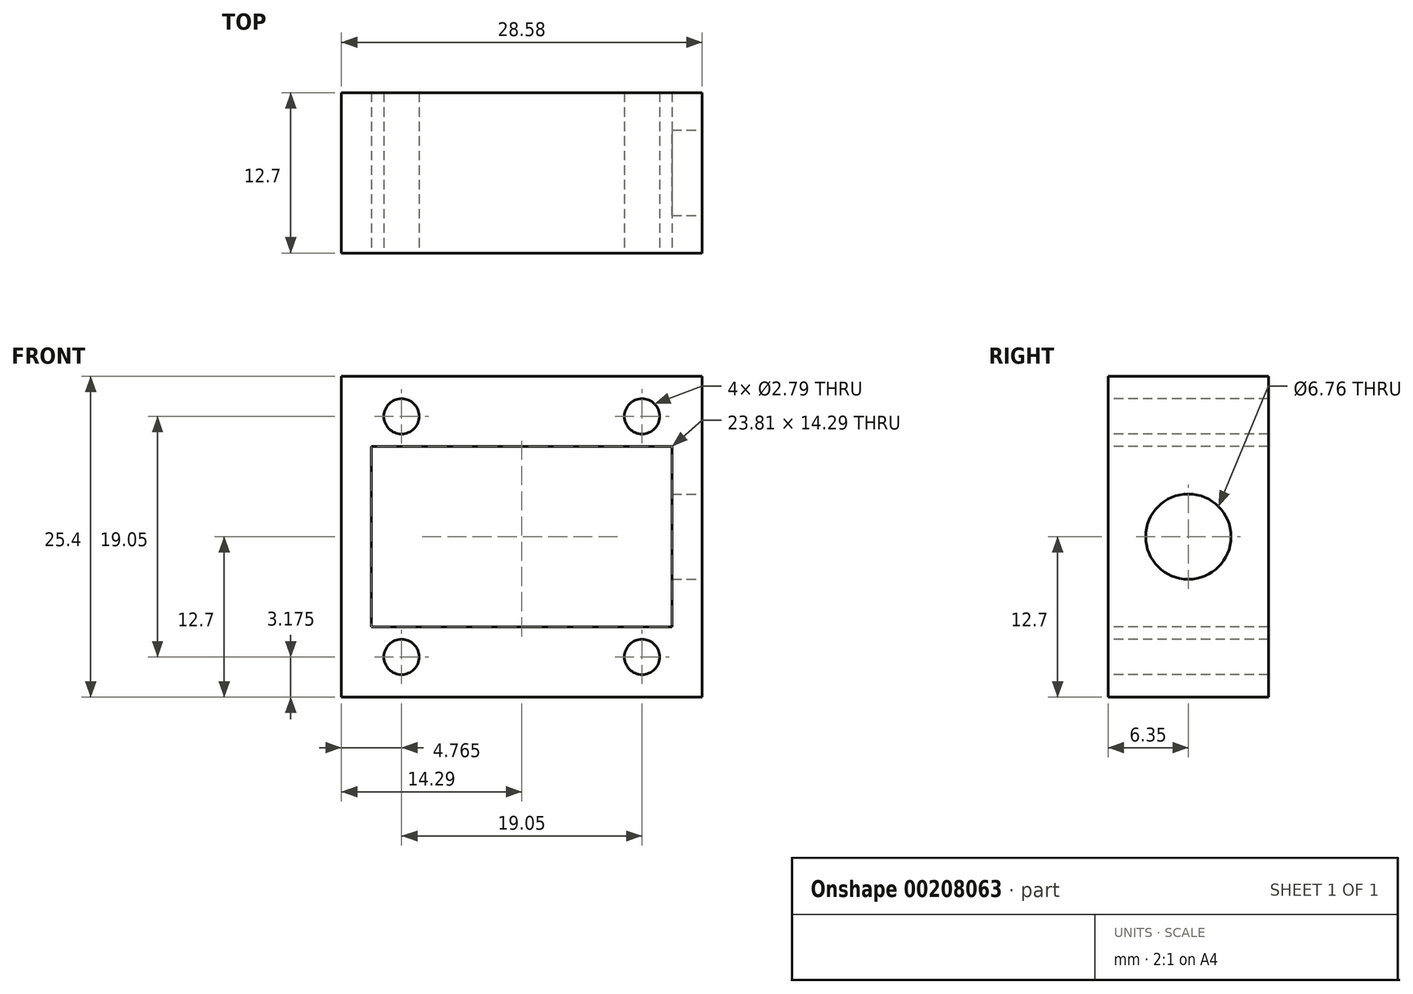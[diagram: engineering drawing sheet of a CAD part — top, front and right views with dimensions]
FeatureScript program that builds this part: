
annotation { "Feature Type Name" : "Feature", "Feature Type Description" : "" }
export const myFeature = defineFeature(function(context is Context, id is Id, definition is map)
    precondition{}
    {
        {
            var Q0;
            Q0=qCreatedBy(makeId("Front.planeOp"),FACE);
            var sketch = newSketch(context, id + "F0", { "sketchPlane" : qUnion([Q0])});
            skLineSegment(sketch, "E0.bottom", {"start": v(14.29, -12.7) * mm, "end": v(-14.29, -12.7) * mm});
            skLineSegment(sketch, "E0.top", {"start": v(14.29, 12.7) * mm, "end": v(-14.29, 12.7) * mm});
            skLineSegment(sketch, "E0.left", {"start": v(14.29, -12.7) * mm, "end": v(14.29, 12.7) * mm});
            skLineSegment(sketch, "E0.right", {"start": v(-14.29, -12.7) * mm, "end": v(-14.29, 12.7) * mm});
            skPoint(sketch, "E0.middle", {"position": v(0, 0) * mm});
            skSolve(sketch);
        }
        {
            var Q0;
            Q0 = qSketchRegion(id + "F0", true);
            extrude(context, id + "F1", {"entities" : qUnion([Q0]), "depth" : 12.7 * mm});
        }
        {
            var Q0;
            Q0=makeQuery(id+"F1.opExtrude","CAP_FACE",FACE,{"disambiguationData":[OSD([sQuery(id+"F0.wireOp",EDGE,"E0.bottom"),sQuery(id+"F0.wireOp",EDGE,"E0.top"),sQuery(id+"F0.wireOp",EDGE,"E0.left"),sQuery(id+"F0.wireOp",EDGE,"E0.right")])],"isStart":false});
            var sketch = newSketch(context, id + "F2", { "sketchPlane" : qUnion([Q0])});
            skLineSegment(sketch, "E1.bottom", {"start": v(11.9, -7.14) * mm, "end": v(-11.9, -7.14) * mm});
            skLineSegment(sketch, "E1.top", {"start": v(11.9, 7.14) * mm, "end": v(-11.9, 7.14) * mm});
            skLineSegment(sketch, "E1.left", {"start": v(11.9, -7.14) * mm, "end": v(11.9, 7.14) * mm});
            skLineSegment(sketch, "E1.right", {"start": v(-11.9, -7.14) * mm, "end": v(-11.9, 7.14) * mm});
            skPoint(sketch, "E1.middle", {"position": v(0, 0) * mm});
            skSolve(sketch);
        }
        {
            var Q0;
            Q0 = qSketchRegion(id + "F2", true);
            extrude(context, id + "F3", {"entities" : qUnion([Q0]), "operationType" : NewBodyOperationType.REMOVE, "endBound" : BoundingType.THROUGH_ALL, "oppositeDirection" : true, "depth" : 25.4 * mm});
        }
        {
            var Q0;
            Q0=makeQuery(id+"F1.opExtrude","SWEPT_FACE",FACE,{"disambiguationData":[OSD([sQuery(id+"F0.wireOp",EDGE,"E0.left")])]});
            var sketch = newSketch(context, id + "F4", { "sketchPlane" : qUnion([Q0])});
            skPoint(sketch, "E2", {"position": v(-6.35, 0) * mm});
            skLineSegment(sketch, "E3", {"start": v(-6.35, 0) * mm, "end": v(0, 0) * mm});
            skLineSegment(sketch, "E4", {"start": v(-6.35, 0) * mm, "end": v(-12.7, 0) * mm});
            skSolve(sketch);
        }
        {
            var Q0;
            Q0=sQuery(id+"F4.wireOp",VERTEX,"E2");
            var Q1;
            Q1=makeQuery(id+"F1.opExtrude","SWEPT_BODY",BODY,{"disambiguationData":[OSD([sQuery(id+"F0.wireOp",EDGE,"E0.bottom"),sQuery(id+"F0.wireOp",EDGE,"E0.top"),sQuery(id+"F0.wireOp",EDGE,"E0.left"),sQuery(id+"F0.wireOp",EDGE,"E0.right")])]});
            hole(context, id + "F5", {"style" : HoleStyle.SIMPLE, "endStyle" : HoleEndStyle.BLIND, "standardTappedOrClearance" : lookupTablePath({ "standard" : "ANSI", "fit" : "Normal (ASME)", "size" : "1/4", "type" : "Clearance" }), "standardBlindInLast" : lookupTablePath({ "fit" : "Free", "standard" : "ANSI", "size" : "1/4", "type" : "Clearance" }), "holeDiameter" : 6.76 * mm, "holeDepth" : 3.97 * mm, "tappedDepth" : 1.59 * mm, "tapClearance" : 3, "locations" : qUnion([Q0]), "scope" : qUnion([Q1])});
        }
        {
            var Q0;
            Q0=makeQuery(id+"F1.opExtrude","CAP_FACE",FACE,{"disambiguationData":[OSD([sQuery(id+"F0.wireOp",EDGE,"E0.bottom"),sQuery(id+"F0.wireOp",EDGE,"E0.top"),sQuery(id+"F0.wireOp",EDGE,"E0.left"),sQuery(id+"F0.wireOp",EDGE,"E0.right")])],"isStart":false});
            var sketch = newSketch(context, id + "F6", { "sketchPlane" : qUnion([Q0])});
            skPoint(sketch, "E5", {"position": v(9.53, -9.52) * mm});
            skPoint(sketch, "E6", {"position": v(-9.53, -9.52) * mm});
            skPoint(sketch, "E7", {"position": v(-9.53, 9.53) * mm});
            skPoint(sketch, "E8", {"position": v(9.53, 9.53) * mm});
            skLineSegment(sketch, "E9", {"start": v(9.53, -9.52) * mm, "end": v(9.53, -12.7) * mm});
            skLineSegment(sketch, "E10", {"start": v(9.53, 9.53) * mm, "end": v(9.53, 12.7) * mm});
            skLineSegment(sketch, "E11", {"start": v(-9.53, -9.53) * mm, "end": v(-14.29, -9.53) * mm});
            skLineSegment(sketch, "E12", {"start": v(9.53, -9.52) * mm, "end": v(14.29, -9.52) * mm});
            skSolve(sketch);
        }
        {
            var Q0;
            Q0=sQuery(id+"F6.wireOp",VERTEX,"E7");
            var Q1;
            Q1=sQuery(id+"F6.wireOp",VERTEX,"E8");
            var Q2;
            Q2=sQuery(id+"F6.wireOp",VERTEX,"E5");
            var Q3;
            Q3=sQuery(id+"F6.wireOp",VERTEX,"E6");
            var Q4;
            Q4=makeQuery(id+"F1.opExtrude","SWEPT_BODY",BODY,{"disambiguationData":[OSD([sQuery(id+"F0.wireOp",EDGE,"E0.bottom"),sQuery(id+"F0.wireOp",EDGE,"E0.top"),sQuery(id+"F0.wireOp",EDGE,"E0.left"),sQuery(id+"F0.wireOp",EDGE,"E0.right")])]});
            hole(context, id + "F7", {"style" : HoleStyle.SIMPLE, "endStyle" : HoleEndStyle.THROUGH, "standardTappedOrClearance" : lookupTablePath({ "standard" : "ANSI", "fit" : "Normal (ASME)", "size" : "#3", "type" : "Clearance" }), "standardBlindInLast" : lookupTablePath({ "fit" : "Free", "standard" : "ANSI", "size" : "#3", "type" : "Clearance" }), "holeDiameter" : 2.8 * mm, "tappedDepth" : 1.6 * mm, "tapClearance" : 3, "locations" : qUnion([Q0, Q1, Q2, Q3]), "scope" : qUnion([Q4])});
        }
    });
